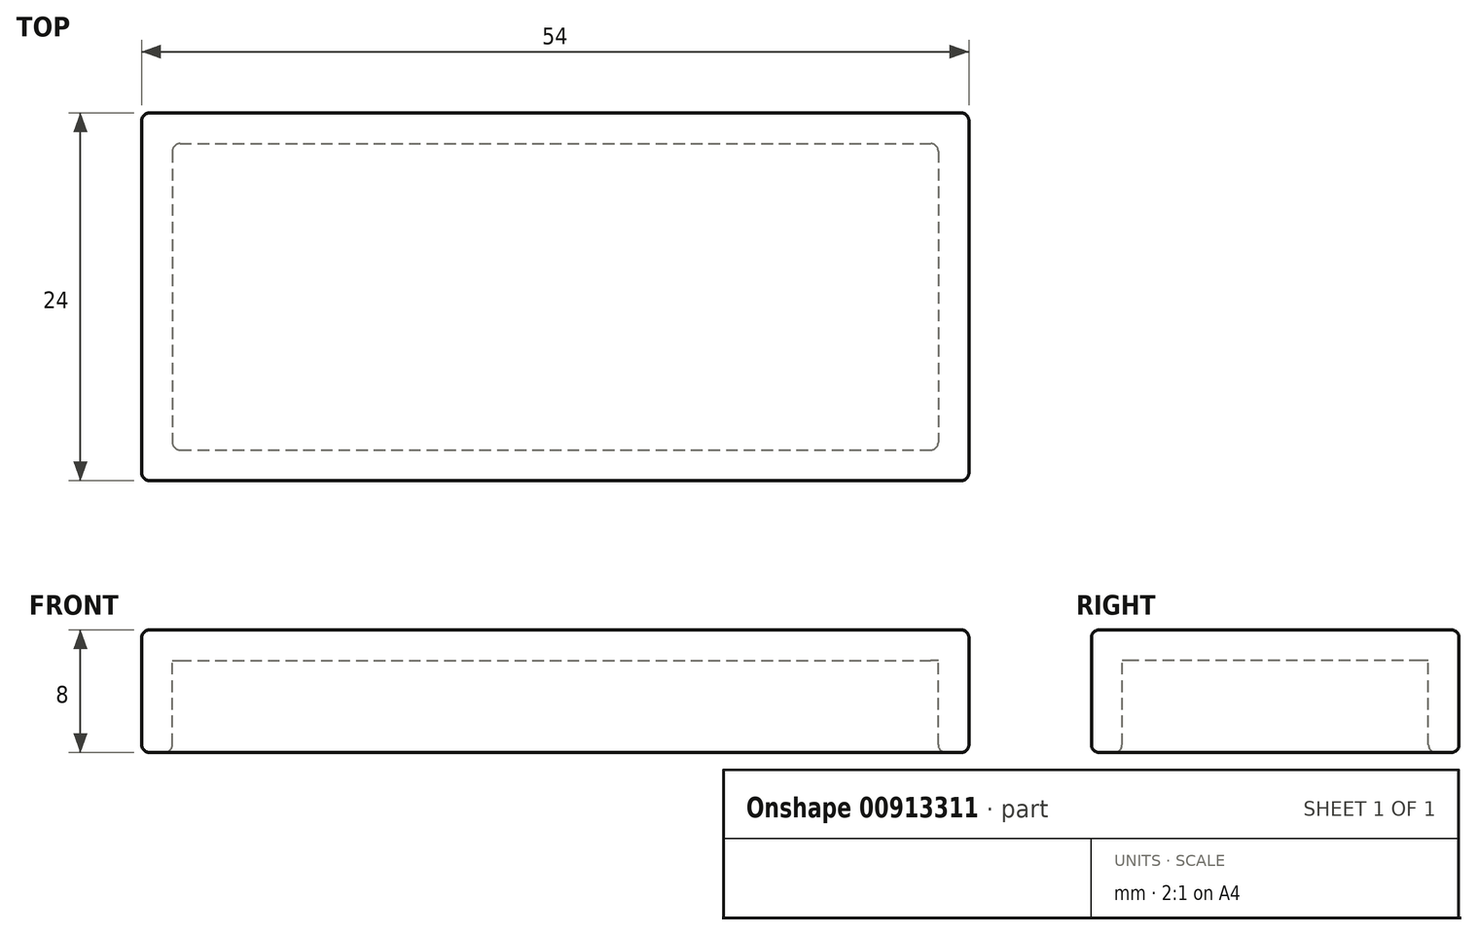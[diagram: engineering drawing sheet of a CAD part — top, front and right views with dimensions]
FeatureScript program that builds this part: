
annotation { "Feature Type Name" : "Feature", "Feature Type Description" : "" }
export const myFeature = defineFeature(function(context is Context, id is Id, definition is map)
    precondition{}
    {
        {
            var Q0;
            Q0=qCreatedBy(makeId("Top.planeOp"),FACE);
            var sketch = newSketch(context, id + "F0", { "sketchPlane" : qUnion([Q0])});
            skLineSegment(sketch, "E0.bottom", {"start": v(-54.28, 34.15) * mm, "end": v(-4.28, 34.15) * mm});
            skLineSegment(sketch, "E0.top", {"start": v(-54.28, 14.15) * mm, "end": v(-4.28, 14.15) * mm});
            skLineSegment(sketch, "E0.left", {"start": v(-54.28, 34.15) * mm, "end": v(-54.28, 14.15) * mm});
            skLineSegment(sketch, "E0.right", {"start": v(-4.28, 34.15) * mm, "end": v(-4.28, 14.15) * mm});
            skSolve(sketch);
        }
        {
            var Q0;
            Q0 = qSketchRegion(id + "F0", true);
            extrude(context, id + "F1", {"entities" : qUnion([Q0]), "depth" : 2 * mm, "offsetDistance" : 25 * mm});
        }
        {
            var Q0;
            Q0=makeQuery(id+"F1.opExtrude","CAP_FACE",FACE,{"disambiguationData":[OSD([sQuery(id+"F0.wireOp",EDGE,"E0.bottom"),sQuery(id+"F0.wireOp",EDGE,"E0.top"),sQuery(id+"F0.wireOp",EDGE,"E0.left"),sQuery(id+"F0.wireOp",EDGE,"E0.right")])],"isStart":false});
            var sketch = newSketch(context, id + "F2", { "sketchPlane" : qUnion([Q0])});
            skLineSegment(sketch, "E1.bottom", {"start": v(-54.28, 34.15) * mm, "end": v(-4.28, 34.15) * mm});
            skLineSegment(sketch, "E1.top", {"start": v(-54.28, 14.15) * mm, "end": v(-4.28, 14.15) * mm});
            skLineSegment(sketch, "E1.left", {"start": v(-54.28, 34.15) * mm, "end": v(-54.28, 14.15) * mm});
            skLineSegment(sketch, "E1.right", {"start": v(-4.28, 34.15) * mm, "end": v(-4.28, 14.15) * mm});
            skLineSegment(sketch, "E2.0", {"start": v(-56.28, 36.15) * mm, "end": v(-56.28, 12.15) * mm});
            skLineSegment(sketch, "E2.1", {"start": v(-2.28, 36.15) * mm, "end": v(-56.28, 36.15) * mm});
            skLineSegment(sketch, "E2.2", {"start": v(-2.28, 12.15) * mm, "end": v(-2.28, 36.15) * mm});
            skLineSegment(sketch, "E2.3", {"start": v(-56.28, 12.15) * mm, "end": v(-2.28, 12.15) * mm});
            skSolve(sketch);
        }
        {
            var Q0;
            Q0 = qSketchRegion(id + "F2", true);
            extrude(context, id + "F3", {"entities" : qUnion([Q0]), "operationType" : NewBodyOperationType.ADD, "oppositeDirection" : true, "depth" : 8 * mm, "offsetDistance" : 25 * mm});
        }
        {
            var Q0;
            Q0=makeQuery(id+"F3.opExtrude","CAP_EDGE",EDGE,{"disambiguationData":[OSD([sQuery(id+"F2.wireOp",EDGE,"E2.3")])],"isStart":false});
            var Q1;
            Q1=makeQuery(id+"F3.opExtrude","CAP_EDGE",EDGE,{"disambiguationData":[OSD([sQuery(id+"F2.wireOp",EDGE,"E1.top")])],"isStart":false});
            var Q2;
            Q2=makeQuery(id+"F3.opExtrude","CAP_EDGE",EDGE,{"disambiguationData":[OSD([sQuery(id+"F2.wireOp",EDGE,"E2.0")])],"isStart":false});
            var Q3;
            Q3=makeQuery(id+"F3.opExtrude","CAP_EDGE",EDGE,{"disambiguationData":[OSD([sQuery(id+"F2.wireOp",EDGE,"E1.left")])],"isStart":false});
            var Q4;
            Q4=makeQuery(id+"F3.opExtrude","CAP_EDGE",EDGE,{"disambiguationData":[OSD([sQuery(id+"F2.wireOp",EDGE,"E2.1")])],"isStart":false});
            var Q5;
            Q5=makeQuery(id+"F3.opExtrude","CAP_EDGE",EDGE,{"disambiguationData":[OSD([sQuery(id+"F2.wireOp",EDGE,"E1.bottom")])],"isStart":false});
            var Q6;
            Q6=makeQuery(id+"F3.opExtrude","CAP_EDGE",EDGE,{"disambiguationData":[OSD([sQuery(id+"F2.wireOp",EDGE,"E1.right")])],"isStart":false});
            var Q7;
            Q7=makeQuery(id+"F3.opExtrude","CAP_EDGE",EDGE,{"disambiguationData":[OSD([sQuery(id+"F2.wireOp",EDGE,"E2.2")])],"isStart":false});
            var Q8;
            Q8=makeQuery(id+"F1.opExtrude","CAP_EDGE",EDGE,{"disambiguationData":[OSD([sQuery(id+"F0.wireOp",EDGE,"E0.right")])],"isStart":true});
            var Q9;
            Q9=makeQuery(id+"F1.opExtrude","CAP_EDGE",EDGE,{"disambiguationData":[OSD([sQuery(id+"F0.wireOp",EDGE,"E0.top")])],"isStart":true});
            var Q10;
            Q10=makeQuery(id+"F3.opExtrude","SWEPT_EDGE",EDGE,{"disambiguationData":[OSD([sQuery(id+"F2.wireOp",EDGE,"E1.top"),sQuery(id+"F2.wireOp",EDGE,"E1.right")])]});
            var Q11;
            Q11=makeQuery(id+"F1.opExtrude","CAP_EDGE",EDGE,{"disambiguationData":[OSD([sQuery(id+"F0.wireOp",EDGE,"E0.bottom")])],"isStart":true});
            var Q12;
            Q12=makeQuery(id+"F3.opExtrude","SWEPT_EDGE",EDGE,{"disambiguationData":[OSD([sQuery(id+"F2.wireOp",EDGE,"E1.bottom"),sQuery(id+"F2.wireOp",EDGE,"E1.right")])]});
            var Q13;
            Q13=makeQuery(id+"F1.opExtrude","CAP_EDGE",EDGE,{"disambiguationData":[OSD([sQuery(id+"F0.wireOp",EDGE,"E0.left")])],"isStart":true});
            var Q14;
            Q14=makeQuery(id+"F3.opExtrude","SWEPT_EDGE",EDGE,{"disambiguationData":[OSD([sQuery(id+"F2.wireOp",EDGE,"E1.bottom"),sQuery(id+"F2.wireOp",EDGE,"E1.left")])]});
            var Q15;
            Q15=makeQuery(id+"F3.opExtrude","SWEPT_EDGE",EDGE,{"disambiguationData":[OSD([sQuery(id+"F2.wireOp",EDGE,"E1.top"),sQuery(id+"F2.wireOp",EDGE,"E1.left")])]});
            var Q16;
            Q16=makeQuery(id+"F3.opExtrude","CAP_EDGE",EDGE,{"disambiguationData":[OSD([sQuery(id+"F2.wireOp",EDGE,"E2.1")])],"isStart":true});
            var Q17;
            Q17=makeQuery(id+"F3.opExtrude","SWEPT_EDGE",EDGE,{"disambiguationData":[OSD([sQuery(id+"F2.wireOp",EDGE,"E2.1"),sQuery(id+"F2.wireOp",EDGE,"E2.2")])]});
            var Q18;
            Q18=makeQuery(id+"F3.opExtrude","CAP_EDGE",EDGE,{"disambiguationData":[OSD([sQuery(id+"F2.wireOp",EDGE,"E2.2")])],"isStart":true});
            var Q19;
            Q19=makeQuery(id+"F3.opExtrude","SWEPT_EDGE",EDGE,{"disambiguationData":[OSD([sQuery(id+"F2.wireOp",EDGE,"E2.2"),sQuery(id+"F2.wireOp",EDGE,"E2.3")])]});
            var Q20;
            Q20=makeQuery(id+"F3.opExtrude","CAP_EDGE",EDGE,{"disambiguationData":[OSD([sQuery(id+"F2.wireOp",EDGE,"E2.3")])],"isStart":true});
            var Q21;
            Q21=makeQuery(id+"F3.opExtrude","SWEPT_EDGE",EDGE,{"disambiguationData":[OSD([sQuery(id+"F2.wireOp",EDGE,"E2.0"),sQuery(id+"F2.wireOp",EDGE,"E2.3")])]});
            var Q22;
            Q22=makeQuery(id+"F3.opExtrude","SWEPT_EDGE",EDGE,{"disambiguationData":[OSD([sQuery(id+"F2.wireOp",EDGE,"E2.0"),sQuery(id+"F2.wireOp",EDGE,"E2.1")])]});
            var Q23;
            Q23=makeQuery(id+"F3.opExtrude","CAP_EDGE",EDGE,{"disambiguationData":[OSD([sQuery(id+"F2.wireOp",EDGE,"E2.0")])],"isStart":true});
            fillet(context, id + "F4", {"entities" : qUnion([Q0, Q1, Q2, Q3, Q4, Q5, Q6, Q7, Q8, Q9, Q10, Q11, Q12, Q13, Q14, Q15, Q16, Q17, Q18, Q19, Q20, Q21, Q22, Q23]), "radius" : 0.5 * mm, "tangentPropagation" : true, "allowEdgeOverflow" : false});
        }
    });
